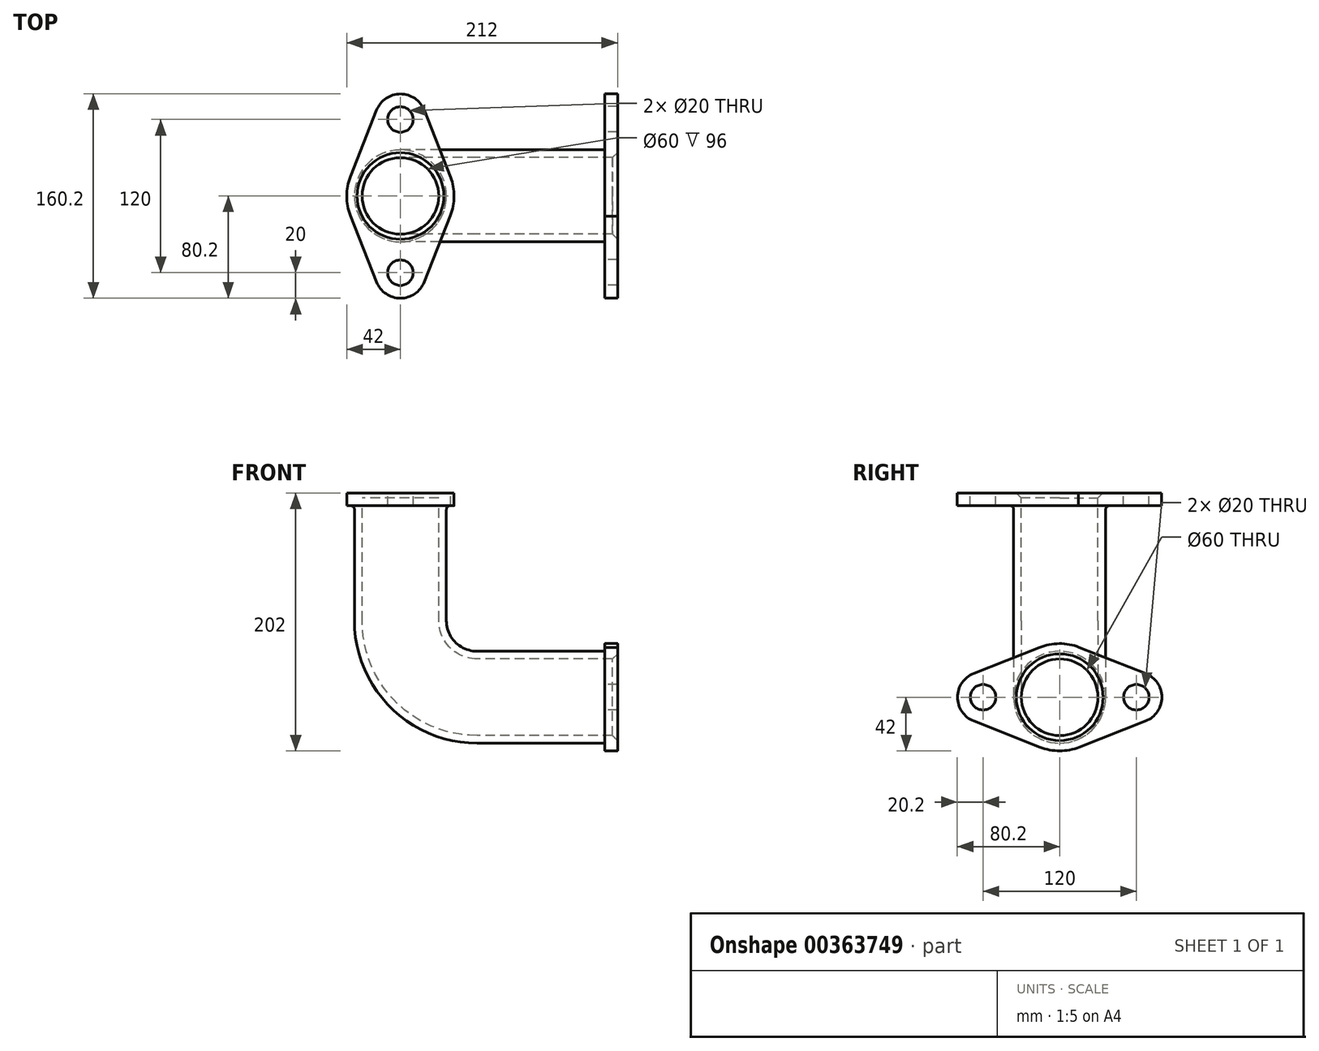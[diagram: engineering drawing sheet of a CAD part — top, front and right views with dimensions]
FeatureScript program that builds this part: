
annotation { "Feature Type Name" : "Feature", "Feature Type Description" : "" }
export const myFeature = defineFeature(function(context is Context, id is Id, definition is map)
    precondition{}
    {
        {
            var Q0;
            Q0=qCreatedBy(makeId("Front.planeOp"),FACE);
            var sketch = newSketch(context, id + "F0", { "sketchPlane" : qUnion([Q0])});
            skLineSegment(sketch, "E0", {"start": v(0, 0) * mm, "end": v(0, 60) * mm, "construction": true});
            skLineSegment(sketch, "E1", {"start": v(0, 0) * mm, "end": v(60, 0) * mm, "construction": true});
            skLineSegment(sketch, "E2", {"start": v(60, 0) * mm, "end": v(160, 0) * mm});
            skLineSegment(sketch, "E3", {"start": v(0, 60) * mm, "end": v(0, 160) * mm});
            skArc(sketch, "E4", {"start": v(0, 60) * mm, "mid": v(17.57, 17.57) * mm, "end": v(60, 0) * mm});
            skSolve(sketch);
        }
        {
            var Q0;
            Q0=qCreatedBy(makeId("Right.planeOp"),FACE);
            var Q1;
            Q1 = qBodyType(qCreatedBy(id + "F2" ,EDGE), BodyType.WIRE);
            cPlane(context, id + "F1", {"entities" : qUnion([Q0, Q1]), "cplaneType" : CPlaneType.OFFSET, "offset" : 160 * mm, "width" : 150 * mm, "height" : 150 * mm});
        }
        {
            var Q0;
            Q0=qCreatedBy(id+"F1.planeOp",FACE);
            var sketch = newSketch(context, id + "F2", { "sketchPlane" : qUnion([Q0])});
            skPoint(sketch, "E5.0", {"position": v(0, 0) * mm});
            skCircle(sketch, "E6", {"center": v(0, 0) * mm, "radius": 30 * mm});
            skCircle(sketch, "E7", {"center": v(0, 0) * mm, "radius": 36 * mm});
            skSolve(sketch);
        }
        {
            var Q0;
            Q0=makeQuery(id+"F2.imprint","IMPRINT",FACE,{"disambiguationData":[TD([[makeQuery(id+"F2.imprint","IMPRINT",EDGE,{"derivedFrom":sQuery(id+"F2.wireOp",EDGE,"E6")}),-1.0]])]});
            var Q1;
            Q1=sQuery(id+"F0.wireOp",EDGE,"E2");
            var Q2;
            Q2=sQuery(id+"F0.wireOp",EDGE,"E4");
            var Q3;
            Q3=sQuery(id+"F0.wireOp",EDGE,"E3");
            sweep(context, id + "F3", {"profiles" : qUnion([Q0]), "path" : qUnion([Q1, Q2, Q3])});
        }
        {
            var Q0;
            Q0=qCreatedBy(id+"F1.planeOp",FACE);
            var sketch = newSketch(context, id + "F4", { "sketchPlane" : qUnion([Q0])});
            skCircle(sketch, "E8.0", {"center": v(0, 0) * mm, "radius": 30 * mm});
            skCircle(sketch, "E9", {"center": v(-60, 0) * mm, "radius": 10 * mm});
            skCircle(sketch, "E10", {"center": v(60, 0) * mm, "radius": 10 * mm});
            skArc(sketch, "E11", {"start": v(-67.33, 18.6) * mm, "mid": v(-80, 0) * mm, "end": v(-67.33, -18.6) * mm});
            skLineSegment(sketch, "E12", {"start": v(-14.8, 39.3) * mm, "end": v(-67.33, 18.6) * mm});
            skLineSegment(sketch, "E13", {"start": v(15.4, 39.07) * mm, "end": v(67.33, 18.6) * mm});
            skLineSegment(sketch, "E14", {"start": v(67.33, -18.6) * mm, "end": v(15.4, -39.07) * mm});
            skLineSegment(sketch, "E15", {"start": v(-67.33, -18.6) * mm, "end": v(-15.4, -39.07) * mm});
            skArc(sketch, "E16.trimOffspring", {"start": v(-15.4, -39.07) * mm, "mid": v(0, -42) * mm, "end": v(15.4, -39.07) * mm});
            skArc(sketch, "E17.trimOffspring", {"start": v(15.4, 39.07) * mm, "mid": v(-0.32, 42) * mm, "end": v(-15.98, 38.84) * mm});
            skArc(sketch, "E18.trimOffspring", {"start": v(67.33, -18.6) * mm, "mid": v(80, 0) * mm, "end": v(67.33, 18.6) * mm});
            skSolve(sketch);
        }
        {
            var Q0;
            Q0 = qSketchRegion(id + "F4", true);
            extrude(context, id + "F5", {"entities" : qUnion([Q0]), "operationType" : NewBodyOperationType.ADD, "depth" : 10 * mm});
        }
        {
            var Q0;
            Q0=qCreatedBy(makeId("Top.planeOp"),FACE);
            cPlane(context, id + "F6", {"entities" : qUnion([Q0]), "cplaneType" : CPlaneType.OFFSET, "offset" : 160 * mm, "width" : 150 * mm, "height" : 150 * mm});
        }
        {
            var Q0;
            Q0=qCreatedBy(id+"F6.planeOp",FACE);
            var sketch = newSketch(context, id + "F7", { "sketchPlane" : qUnion([Q0])});
            skPoint(sketch, "E19", {"position": v(0, 0) * mm});
            skCircle(sketch, "E20.0", {"center": v(0, -0.2) * mm, "radius": 30 * mm});
            skCircle(sketch, "E21", {"center": v(0, 59.8) * mm, "radius": 10 * mm});
            skCircle(sketch, "E22", {"center": v(0, -60.2) * mm, "radius": 10 * mm});
            skArc(sketch, "E23", {"start": v(18.6, 67.13) * mm, "mid": v(0, 79.8) * mm, "end": v(-18.6, 67.13) * mm});
            skLineSegment(sketch, "E24", {"start": v(39.3, 14.6) * mm, "end": v(18.6, 67.13) * mm});
            skLineSegment(sketch, "E25", {"start": v(39.07, -15.6) * mm, "end": v(18.6, -67.53) * mm});
            skLineSegment(sketch, "E26", {"start": v(-18.6, -67.53) * mm, "end": v(-39.07, -15.6) * mm});
            skLineSegment(sketch, "E27", {"start": v(-18.6, 67.13) * mm, "end": v(-39.07, 15.2) * mm});
            skArc(sketch, "E28.trimOffspring", {"start": v(-39.07, 15.2) * mm, "mid": v(-42, -0.2) * mm, "end": v(-39.07, -15.6) * mm});
            skArc(sketch, "E29.trimOffspring", {"start": v(39.07, -15.6) * mm, "mid": v(42, 0.12) * mm, "end": v(38.84, 15.78) * mm});
            skArc(sketch, "E30.trimOffspring", {"start": v(-18.6, -67.53) * mm, "mid": v(0, -80.2) * mm, "end": v(18.6, -67.53) * mm});
            skSolve(sketch);
        }
        {
            var Q0;
            Q0=makeQuery(id+"F7.imprint","IMPRINT",FACE,{"disambiguationData":[TD([[makeQuery(id+"F7.imprint","IMPRINT",EDGE,{"derivedFrom":sQuery(id+"F7.wireOp",EDGE,"E20.0")}),-1.0]])]});
            extrude(context, id + "F8", {"entities" : qUnion([Q0]), "operationType" : NewBodyOperationType.ADD, "oppositeDirection" : true, "depth" : 10 * mm});
        }
        {
            var Q0;
            Q0=makeQuery(id+"F8.boolean.opBoolean","INTERSECT",EDGE,{"derivedFrom":[makeQuery(id+"F3.opSweep","SWEPT_FACE",FACE,{"disambiguationData":[OSD([sQuery(id+"F0.wireOp",EDGE,"E3"),sQuery(id+"F2.wireOp",EDGE,"E7")])]}),makeQuery(id+"F8.opExtrude","CAP_FACE",FACE,{"disambiguationData":[OSD([sQuery(id+"F7.wireOp",EDGE,"E20.0"),sQuery(id+"F7.wireOp",EDGE,"E21"),sQuery(id+"F7.wireOp",EDGE,"E22"),sQuery(id+"F7.wireOp",EDGE,"E23"),sQuery(id+"F7.wireOp",EDGE,"E24"),sQuery(id+"F7.wireOp",EDGE,"E25"),sQuery(id+"F7.wireOp",EDGE,"E26"),sQuery(id+"F7.wireOp",EDGE,"E27"),sQuery(id+"F7.wireOp",EDGE,"E28.trimOffspring"),sQuery(id+"F7.wireOp",EDGE,"E29.trimOffspring"),sQuery(id+"F7.wireOp",EDGE,"E30.trimOffspring")])],"isStart":false})]});
            var Q1;
            Q1=makeQuery(id+"F3.opSweep","CAP_EDGE",EDGE,{"disambiguationData":[OSD([sQuery(id+"F0.wireOp",VERTEX,"E2.end"),sQuery(id+"F2.wireOp",EDGE,"E7")])],"isStart":true});
            fillet(context, id + "F9", {"entities" : qUnion([Q0, Q1]), "radius" : 3 * mm, "tangentPropagation" : true, "allowEdgeOverflow" : false});
        }
        {
            var Q0;
            Q0=makeQuery(id+"F3.opSweep","CAP_EDGE",EDGE,{"disambiguationData":[OSD([sQuery(id+"F0.wireOp",VERTEX,"E3.end"),sQuery(id+"F2.wireOp",EDGE,"E6")])],"isStart":false});
            var Q1;
            Q1=makeQuery(id+"F8.opExtrude","CAP_EDGE",EDGE,{"disambiguationData":[OSD([sQuery(id+"F7.wireOp",EDGE,"E20.0")])],"isStart":true});
            var Q2;
            Q2=makeQuery(id+"F5.opExtrude","CAP_EDGE",EDGE,{"disambiguationData":[OSD([sQuery(id+"F4.wireOp",EDGE,"E8.0")])],"isStart":false});
            chamfer(context, id + "F10", {"entities" : qUnion([Q0, Q1, Q2]), "width" : 4 * mm, "tangentPropagation" : true});
        }
    });
